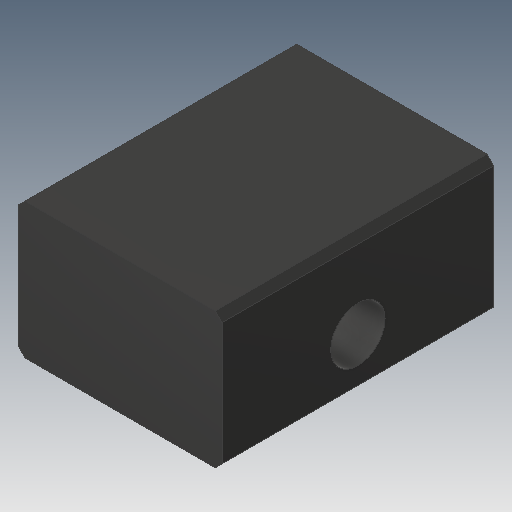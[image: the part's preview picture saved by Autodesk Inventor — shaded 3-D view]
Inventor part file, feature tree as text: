
AUTODESK INVENTOR PART (.ipt)
format: ipt  version: 2018 (Build 220112000, 112)  size: 100,352 bytes
history: native  units: in
note: dims shown in document units (in); Inventor stores cm internally (conversion verified against a paired STEP export)
features: other x3, sketch x1
ambient origin geometry x8: Origin, YZ Plane, XZ Plane, XY Plane, X Axis, Y Axis, Z Axis, Center Point
bodies: Solid1 (feature_tree)
feature tree (4):
  other  "10-006-ACTR-FIX_MIR.ipt"
  other  "Solid1::10-006-ACTR-FIX_MIR.ipt"
  other  "TaggingFeature1"
  sketch  "Sketch1"  dims[d0=0.3937in]
